# Revit family: ALPHI_PP_R
name_source: partatom
category: Equipement spécialisé
units: mm (PartAtom-declared; Revit-internal decimal feet)

## family parameters
Autoriser la découpe dans les vues = Non
Basée sur le plan de construction = Non
Conserver l'orientation des annotations = Non
Cote de connecteur circulaire = Utiliser le diamètre
Couper avec des vides une fois chargée = Non
Partagée = Non
Repère de localisation dans la pièce = Non
Toujours verticalement = Oui
Type d'élément = Normal

## types (4) — shared parameters
ALPHI_FOR_V = 20.00 kN
ALPHI_INE_I = 695.00 cm⁴
ALPHI_LG_HAUTEUR ENCOMBREMENT = 18 cm
ALPHI_LG_LARGEUR = 14.6 cm
ALPHI_MOM_M = 11.00 kN-m
ALPHI_PRE_E = 69000.0 MPa
ALPHI_TXT_NOMENCLATURE_GAMME = Poutrelles primaires
LG_DECALAGE AXE = 5 cm
LG_LARGEUR ATTACHE = 10 cm
zero-valued in all types: Elévation par défaut

## per-type parameters (varying)
| type | ALPHI_LG_LONGUEUR | ALPHI_MAS_POIDS | ALPHI_MAT_MATERIAU COULEUR TYPE | ALPHI_TXT_DESIGNATION | ALPHI_TXT_NOMENCLATURE_ABREVIATION | ALPHI_TXT_NOMENCLATURE_DESIGNATION | ALPHI_VIS_VISIBILITE PP 090 | ALPHI_VIS_VISIBILITE PP 110 | ALPHI_VIS_VISIBILITE PP 150 | ALPHI_VIS_VISIBILITE PP 180 | LG_LONGUEUR ENTRAXE |
| PP090 R | 90 cm | 14.42 kg | ALPHI_acier_laque_magenta | PP090 | PP090 | Poutrelle primaire 90cm | Oui | Non | Non | Non | 100 cm |
| PP110 R | 110 cm | 7.68 kg | ALPHI_acier_laque_noir | PP110 | PP110 | Poutrelle primaire 110cm | Non | Oui | Non | Non | 120 cm |
| PP150 R | 150 cm | 10.44 kg | ALPHI_acier_laque_vert_fonce | PP150 | PP150 | Poutrelle primaire 150cm | Non | Non | Oui | Non | 160 cm |
| PP180 R | 180 cm | 14.42 kg | ALPHI_acier_laque_cyan | PP180 | PP180 | Poutrelle primaire 180cm | Non | Non | Non | Oui | 190 cm |

## geometry (parser evidence)
native form markers: Blend x2
no freeform markers — native parametric forms only
